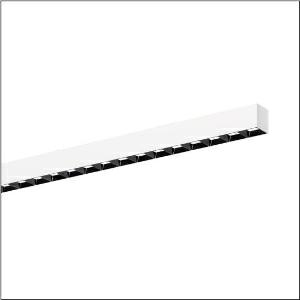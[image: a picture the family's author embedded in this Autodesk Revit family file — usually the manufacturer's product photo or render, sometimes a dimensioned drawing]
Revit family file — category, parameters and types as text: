
# Revit family: silica_r__21_51mx21tctaw_c13c
name_source: partatom
category: Lighting Fixtures
units: mm (PartAtom-declared; Revit-internal decimal feet)

## family parameters
Cut with Voids When Loaded = No
Host = Face
Light Source = No
Part Type = Normal
Room Calculation Point = No
Round Connector Dimension = Use Diameter
Shared = No

## types (1)
- --- (1 x LED, 9300 lm, 80.5 W, 6500K)
    Apparent Load = 81 VA
    CIE Flux Codes = 85 99 100 100 100
    Color Rendering = 80
    Color Temperature = 6500K
    Default Elevation = 1800 mm
    Description = Silica® 21, office luminaire, primary light control with darklight reflector, of PMMA, black, CAT 2 (L<= 3000cd/m²), light emission: direct distribution, primary light characteristic: symmetric, installation type: surface-mounted, LED, rated luminous flux: 9.300lm, luminous efficacy: 110lm/W, light colour: 8tw, colour temperature: 2700..6500K, control gear: ECG DALI, with terminal, 3+2-pole, max. 2.5mm², mains connection: 220..240V, AC, 50/60Hz, rated input power: 84.6W, luminaire housing, of aluminium, traffic white (RAL 9016), length: 3.004mm, width: 53mm, height: 53mm, protection rating (complete): IP20, insulation class (complete): insulation class I (protective earthing), certification: CE, permissible operating ambient temperature: 0..+35°C, standard: EN 50419, packaging unit: 1 piece
    Height = 0 mm  [stored 0 ft]
    Lamp = 1 x LED
    Lamp Light Flux = 9300 lm
    Lamp Power = 80.5 W
    Lamp count = 1
    Length = 3004 mm
    Luminous efficacy = 116 lm/W
    Manufacturer = Siteco
    ModVariant = No
    Model = 51MX21TCTAW
    Mounting Place = Ceiling
    Mounting Type = Recessed
    Number of Poles = 1
    OnlyDefault = Yes
    Power Factor = 1
    Product Name = Silica® 21
    Product group = office luminaire | ceiling recessed
    ProductGroupID = 401
    Protection Class = Protection class I
    Protection Degree = IP 20
    RLX_Detail_Level = 1
    RLX_Emergency_Light_Flux = 0 lm
    RLX_Emergency_Type = 0
    RLX_Emergency_Type_DB = No
    RlxData = <blob elided: 58521 chars, md5=03d3de74>
    Socket = socket
    Standby Power = 0 W
    System Light Flux = 9300 lm
    System Power = 81 W
    Type Comments = individual setting
    Type Image = l_1297779.jpg
    URL = http://relux.com
    VarID = @adj_071401
    Voltage = 0 V
    Weight = 0.00 kg
    Width = 53 mm

note: [stored X ft] marks values corroborated as IEEE doubles in the binary element streams (Revit-internal decimal feet)

## geometry (parser evidence)
native form markers: Blend x4, Sweep x12
no freeform markers — native parametric forms only
